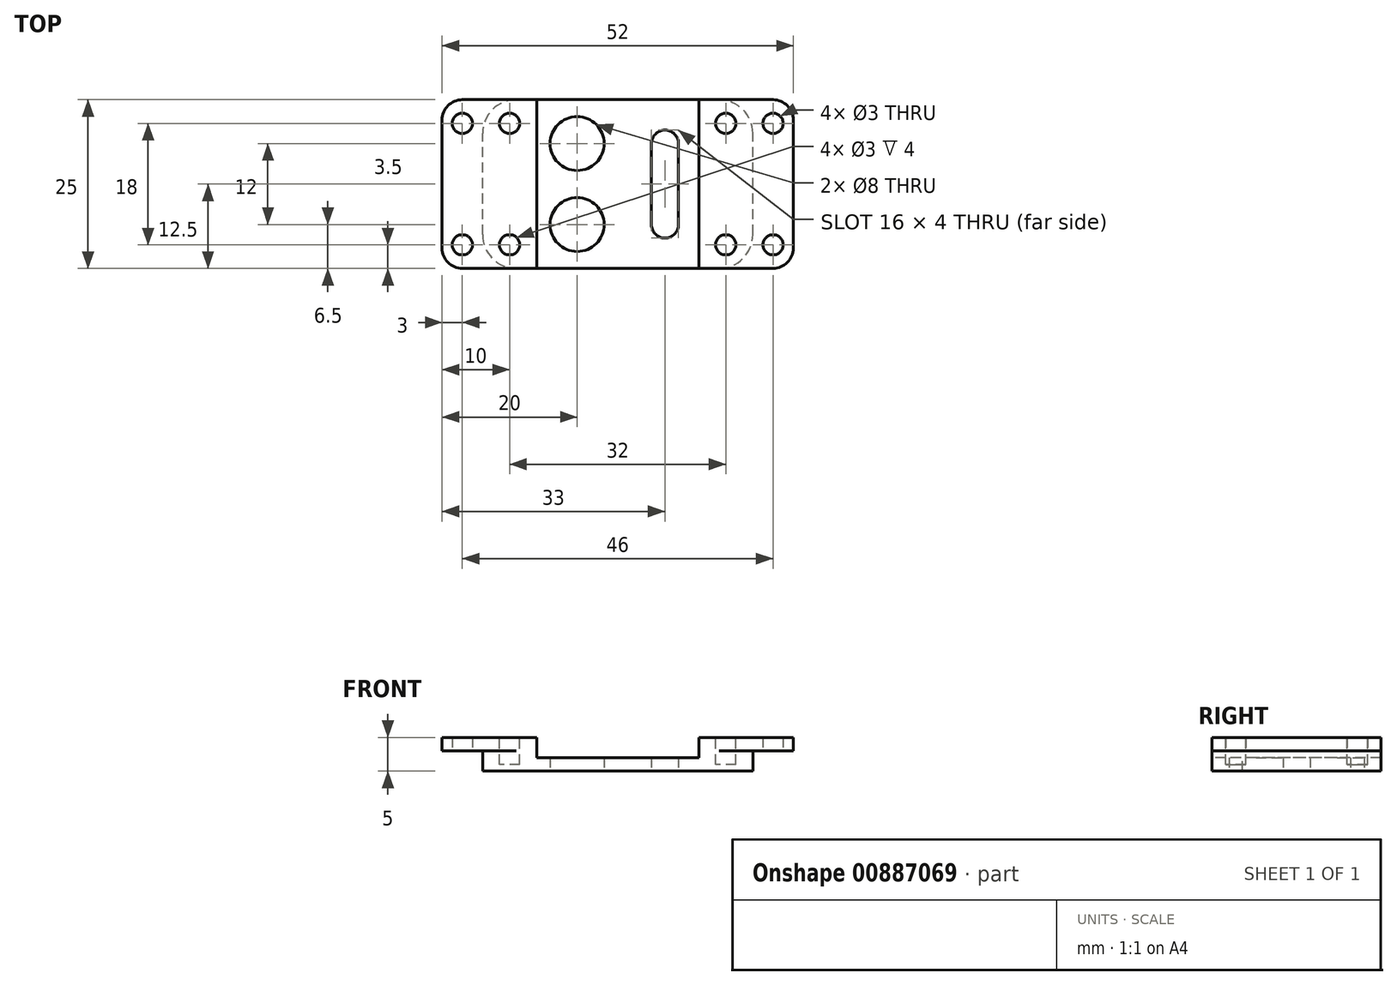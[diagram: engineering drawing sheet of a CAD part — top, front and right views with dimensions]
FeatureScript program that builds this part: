
annotation { "Feature Type Name" : "Feature", "Feature Type Description" : "" }
export const myFeature = defineFeature(function(context is Context, id is Id, definition is map)
    precondition{}
    {
        {
            var Q0;
            Q0=qCreatedBy(makeId("Top.planeOp"),FACE);
            var sketch = newSketch(context, id + "F0", { "sketchPlane" : qUnion([Q0])});
            skLineSegment(sketch, "E0.bottom", {"start": v(20, -12.5) * mm, "end": v(-20, -12.5) * mm});
            skLineSegment(sketch, "E0.top", {"start": v(20, 12.5) * mm, "end": v(-20, 12.5) * mm});
            skLineSegment(sketch, "E0.left", {"start": v(20, -12.5) * mm, "end": v(20, 12.5) * mm});
            skLineSegment(sketch, "E0.right", {"start": v(-20, -12.5) * mm, "end": v(-20, 12.5) * mm});
            skPoint(sketch, "E0.middle", {"position": v(0, 0) * mm});
            skSolve(sketch);
        }
        {
            var Q0;
            Q0=makeQuery(id+"F0.imprint","IMPRINT",FACE,{"disambiguationData":[TD([[makeQuery(id+"F0.imprint","IMPRINT",EDGE,{"derivedFrom":sQuery(id+"F0.wireOp",EDGE,"E0.bottom")}),-1.0]])]});
            extrude(context, id + "F1", {"entities" : qUnion([Q0]), "depth" : 3 * mm, "offsetDistance" : 25 * mm});
        }
        {
            var Q0;
            Q0=makeQuery(id+"F1.opExtrude","SWEPT_EDGE",EDGE,{"disambiguationData":[OSD([sQuery(id+"F0.wireOp",EDGE,"E0.bottom"),sQuery(id+"F0.wireOp",EDGE,"E0.right")])]});
            var Q1;
            Q1=makeQuery(id+"F1.opExtrude","SWEPT_EDGE",EDGE,{"disambiguationData":[OSD([sQuery(id+"F0.wireOp",EDGE,"E0.top"),sQuery(id+"F0.wireOp",EDGE,"E0.right")])]});
            var Q2;
            Q2=makeQuery(id+"F1.opExtrude","SWEPT_EDGE",EDGE,{"disambiguationData":[OSD([sQuery(id+"F0.wireOp",EDGE,"E0.bottom"),sQuery(id+"F0.wireOp",EDGE,"E0.left")])]});
            var Q3;
            Q3=makeQuery(id+"F1.opExtrude","SWEPT_EDGE",EDGE,{"disambiguationData":[OSD([sQuery(id+"F0.wireOp",EDGE,"E0.top"),sQuery(id+"F0.wireOp",EDGE,"E0.left")])]});
            fillet(context, id + "F2", {"entities" : qUnion([Q0, Q1, Q2, Q3]), "radius" : 5 * mm, "tangentPropagation" : true, "allowEdgeOverflow" : false});
        }
        {
            var Q0;
            Q0=makeQuery(id+"F1.opExtrude","CAP_FACE",FACE,{"disambiguationData":[OSD([sQuery(id+"F0.wireOp",EDGE,"E0.bottom"),sQuery(id+"F0.wireOp",EDGE,"E0.top"),sQuery(id+"F0.wireOp",EDGE,"E0.left"),sQuery(id+"F0.wireOp",EDGE,"E0.right")])],"isStart":false});
            var sketch = newSketch(context, id + "F3", { "sketchPlane" : qUnion([Q0])});
            skLineSegment(sketch, "E1.bottom", {"start": v(-26, -12.5) * mm, "end": v(26, -12.5) * mm});
            skLineSegment(sketch, "E1.top", {"start": v(-26, 12.5) * mm, "end": v(26, 12.5) * mm});
            skLineSegment(sketch, "E1.left", {"start": v(-26, -12.5) * mm, "end": v(-26, 12.5) * mm});
            skLineSegment(sketch, "E1.right", {"start": v(26, -12.5) * mm, "end": v(26, 12.5) * mm});
            skPoint(sketch, "E1.middle", {"position": v(0, 0) * mm});
            skSolve(sketch);
        }
        {
            var Q0;
            Q0=qSketchRegion(id+"F3",true);
            extrude(context, id + "F4", {"entities" : qUnion([Q0]), "operationType" : NewBodyOperationType.ADD, "depth" : 2 * mm, "offsetDistance" : 25 * mm});
        }
        {
            var Q0;
            Q0=makeQuery(id+"F4.opExtrude","SWEPT_EDGE",EDGE,{"disambiguationData":[OSD([sQuery(id+"F3.wireOp",EDGE,"E1.top"),sQuery(id+"F3.wireOp",EDGE,"E1.right")])]});
            var Q1;
            Q1=makeQuery(id+"F4.opExtrude","SWEPT_EDGE",EDGE,{"disambiguationData":[OSD([sQuery(id+"F3.wireOp",EDGE,"E1.bottom"),sQuery(id+"F3.wireOp",EDGE,"E1.right")])]});
            var Q2;
            Q2=makeQuery(id+"F4.opExtrude","SWEPT_EDGE",EDGE,{"disambiguationData":[OSD([sQuery(id+"F3.wireOp",EDGE,"E1.bottom"),sQuery(id+"F3.wireOp",EDGE,"E1.left")])]});
            var Q3;
            Q3=makeQuery(id+"F4.opExtrude","SWEPT_EDGE",EDGE,{"disambiguationData":[OSD([sQuery(id+"F3.wireOp",EDGE,"E1.top"),sQuery(id+"F3.wireOp",EDGE,"E1.left")])]});
            fillet(context, id + "F5", {"entities" : qUnion([Q0, Q1, Q2, Q3]), "radius" : 3 * mm, "tangentPropagation" : true, "allowEdgeOverflow" : false});
        }
        {
            var Q0;
            Q0=qCreatedBy(makeId("Top.planeOp"),FACE);
            var sketch = newSketch(context, id + "F6", { "sketchPlane" : qUnion([Q0])});
            skCircle(sketch, "E2", {"center": v(23, 9) * mm, "radius": 1.5 * mm});
            skCircle(sketch, "E3", {"center": v(23, -9) * mm, "radius": 1.5 * mm});
            skCircle(sketch, "E4", {"center": v(-23, -9) * mm, "radius": 1.5 * mm});
            skCircle(sketch, "E5", {"center": v(-23, 9) * mm, "radius": 1.5 * mm});
            skLineSegment(sketch, "E6.bottom", {"start": v(23, 9) * mm, "end": v(-23, 9) * mm, "construction": true});
            skLineSegment(sketch, "E6.top", {"start": v(23, -9) * mm, "end": v(-23, -9) * mm, "construction": true});
            skLineSegment(sketch, "E6.left", {"start": v(23, 9) * mm, "end": v(23, -9) * mm, "construction": true});
            skLineSegment(sketch, "E6.right", {"start": v(-23, 9) * mm, "end": v(-23, -9) * mm, "construction": true});
            skPoint(sketch, "E6.middle", {"position": v(0, 0) * mm});
            skSolve(sketch);
        }
        {
            var Q0;
            Q0=qSketchRegion(id+"F6",true);
            extrude(context, id + "F7", {"entities" : qUnion([Q0]), "operationType" : NewBodyOperationType.REMOVE, "depth" : 25 * mm, "offsetDistance" : 25 * mm});
        }
        {
            var Q0;
            Q0=makeQuery(id+"F4.opExtrude","CAP_FACE",FACE,{"disambiguationData":[OSD([sQuery(id+"F3.wireOp",EDGE,"E1.bottom"),sQuery(id+"F3.wireOp",EDGE,"E1.top"),sQuery(id+"F3.wireOp",EDGE,"E1.left"),sQuery(id+"F3.wireOp",EDGE,"E1.right")])],"isStart":false});
            var sketch = newSketch(context, id + "F8", { "sketchPlane" : qUnion([Q0])});
            skLineSegment(sketch, "E7.bottom", {"start": v(-16, -9) * mm, "end": v(16, -9) * mm, "construction": true});
            skLineSegment(sketch, "E7.top", {"start": v(-16, 9) * mm, "end": v(16, 9) * mm, "construction": true});
            skLineSegment(sketch, "E7.left", {"start": v(-16, -9) * mm, "end": v(-16, 9) * mm, "construction": true});
            skLineSegment(sketch, "E7.right", {"start": v(16, -9) * mm, "end": v(16, 9) * mm, "construction": true});
            skPoint(sketch, "E7.middle", {"position": v(0, 0) * mm});
            skCircle(sketch, "E8", {"center": v(16, -9) * mm, "radius": 1.5 * mm});
            skCircle(sketch, "E9", {"center": v(-16, -9) * mm, "radius": 1.5 * mm});
            skCircle(sketch, "E10", {"center": v(-16, 9) * mm, "radius": 1.5 * mm});
            skCircle(sketch, "E11", {"center": v(16, 9) * mm, "radius": 1.5 * mm});
            skSolve(sketch);
        }
        {
            var Q0;
            Q0=qSketchRegion(id+"F8",true);
            extrude(context, id + "F9", {"entities" : qUnion([Q0]), "operationType" : NewBodyOperationType.REMOVE, "oppositeDirection" : true, "depth" : 4 * mm, "offsetDistance" : 25 * mm});
        }
        {
            var Q0;
            Q0=makeQuery(id+"F4.opExtrude","CAP_FACE",FACE,{"disambiguationData":[OSD([sQuery(id+"F3.wireOp",EDGE,"E1.bottom"),sQuery(id+"F3.wireOp",EDGE,"E1.top"),sQuery(id+"F3.wireOp",EDGE,"E1.left"),sQuery(id+"F3.wireOp",EDGE,"E1.right")])],"isStart":false});
            var sketch = newSketch(context, id + "F10", { "sketchPlane" : qUnion([Q0])});
            skLineSegment(sketch, "E12.bottom", {"start": v(-12, 12.5) * mm, "end": v(12, 12.5) * mm});
            skLineSegment(sketch, "E12.top", {"start": v(-12, -12.5) * mm, "end": v(12, -12.5) * mm});
            skLineSegment(sketch, "E12.left", {"start": v(-12, 12.5) * mm, "end": v(-12, -12.5) * mm});
            skLineSegment(sketch, "E12.right", {"start": v(12, 12.5) * mm, "end": v(12, -12.5) * mm});
            skSolve(sketch);
        }
        {
            var Q0;
            Q0=makeQuery(id+"F10.imprint","IMPRINT",FACE,{"disambiguationData":[TD([[makeQuery(id+"F10.imprint","IMPRINT",EDGE,{"derivedFrom":sQuery(id+"F10.wireOp",EDGE,"E12.bottom")}),-1.0]])]});
            extrude(context, id + "F11", {"entities" : qUnion([Q0]), "operationType" : NewBodyOperationType.REMOVE, "oppositeDirection" : true, "depth" : 3 * mm, "offsetDistance" : 25 * mm});
        }
        {
            var Q0;
            Q0=makeQuery(id+"F1.opExtrude","CAP_FACE",FACE,{"disambiguationData":[OSD([sQuery(id+"F0.wireOp",EDGE,"E0.bottom"),sQuery(id+"F0.wireOp",EDGE,"E0.top"),sQuery(id+"F0.wireOp",EDGE,"E0.left"),sQuery(id+"F0.wireOp",EDGE,"E0.right")])],"isStart":true});
            var sketch = newSketch(context, id + "F12", { "sketchPlane" : qUnion([Q0])});
            skLineSegment(sketch, "E13.bottom", {"start": v(5, 8) * mm, "end": v(9, 8) * mm});
            skLineSegment(sketch, "E13.top", {"start": v(5, -8) * mm, "end": v(9, -8) * mm});
            skLineSegment(sketch, "E13.left", {"start": v(5, 8) * mm, "end": v(5, -8) * mm});
            skLineSegment(sketch, "E13.right", {"start": v(9, 8) * mm, "end": v(9, -8) * mm});
            skCircle(sketch, "E14", {"center": v(-6, -6) * mm, "radius": 4 * mm});
            skCircle(sketch, "E15", {"center": v(-6, 6) * mm, "radius": 4 * mm});
            skSolve(sketch);
        }
        {
            var Q0;
            Q0=qSketchRegion(id+"F12",true);
            extrude(context, id + "F13", {"entities" : qUnion([Q0]), "operationType" : NewBodyOperationType.REMOVE, "oppositeDirection" : true, "depth" : 25 * mm, "offsetDistance" : 25 * mm});
        }
        {
            var Q0;
            Q0=makeQuery(id+"F13.boolean.opBoolean","COPY",EDGE,{"derivedFrom":makeQuery(id+"F13.opExtrude","SWEPT_EDGE",EDGE,{"disambiguationData":[OSD([sQuery(id+"F12.wireOp",EDGE,"E13.top"),sQuery(id+"F12.wireOp",EDGE,"E13.right")])]})});
            var Q1;
            Q1=makeQuery(id+"F13.boolean.opBoolean","COPY",EDGE,{"derivedFrom":makeQuery(id+"F13.opExtrude","SWEPT_EDGE",EDGE,{"disambiguationData":[OSD([sQuery(id+"F12.wireOp",EDGE,"E13.top"),sQuery(id+"F12.wireOp",EDGE,"E13.left")])]})});
            var Q2;
            Q2=makeQuery(id+"F13.boolean.opBoolean","COPY",EDGE,{"derivedFrom":makeQuery(id+"F13.opExtrude","SWEPT_EDGE",EDGE,{"disambiguationData":[OSD([sQuery(id+"F12.wireOp",EDGE,"E13.bottom"),sQuery(id+"F12.wireOp",EDGE,"E13.right")])]})});
            var Q3;
            Q3=makeQuery(id+"F13.boolean.opBoolean","COPY",EDGE,{"derivedFrom":makeQuery(id+"F13.opExtrude","SWEPT_EDGE",EDGE,{"disambiguationData":[OSD([sQuery(id+"F12.wireOp",EDGE,"E13.bottom"),sQuery(id+"F12.wireOp",EDGE,"E13.left")])]})});
            fillet(context, id + "F14", {"entities" : qUnion([Q0, Q1, Q2, Q3]), "radius" : 2 * mm, "tangentPropagation" : true, "allowEdgeOverflow" : false});
        }
    });
